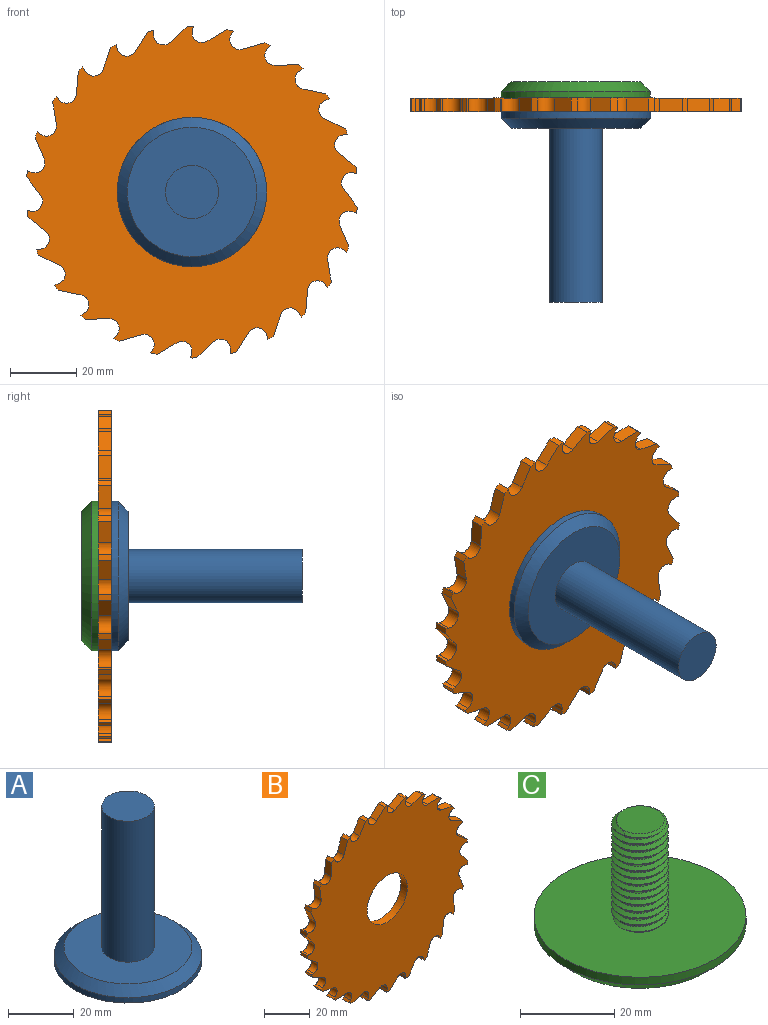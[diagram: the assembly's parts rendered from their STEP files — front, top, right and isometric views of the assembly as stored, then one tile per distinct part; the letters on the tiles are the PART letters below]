
ASSEMBLY  parts=3 mates=4
PART A: 15 faces, bbox 45.5x45.5x61.2 mm
  f0: plane 25.52x25.52mm, normal (0,0,-1), area 393.9mm2, adj f1,f9,f10,f11,f13
  f1: cylinder r=12.5mm len=25mm, axis (0,0,-1), area 196.3mm2, adj f0,f7
  f2: cone r=6mm half-angle=60deg, axis (0,0,-1), area 130.6mm2, adj f8,f12
  f3: plane 16x16mm, normal (0,0,1), area 201.1mm2, adj f4
  f4: cylinder r=8mm len=52.5mm, axis (0,0,-1), area 2638.9mm2, adj f3,f5
  f5: plane 39x39mm, normal (0,0,1), area 993.5mm2, adj f4,f14
  f6: cylinder r=22.5mm len=45mm, axis (0,0,-1), area 282.7mm2, adj f7,f14
  f7: plane 45x45mm, normal (0,0,-1), area 1099.6mm2, adj f1,f6
  f8: plane 6.23x1.47mm, normal (0,0,-1), area 0.6mm2, adj f2,f9,f10,f11
  f9: bspline ~31.17x14.02mm, area 657.5mm2, adj f0,f8,f11,f12,f13
  f10: bspline ~31.46x14.02mm, area 661.4mm2, adj f0,f8,f11,f12,f13
  f11: bspline ~30.55x14.21mm, area 166.2mm2, adj f0,f8,f9,f10
  f12: plane 12.44x11.91mm, normal (0,0,1), area 16.7mm2, adj f2,f9,f10,f13
  f13: cylinder r=5.12mm len=30mm, axis (0,0,1), area 392.2mm2, adj f0,f9,f10,f12
  f14: cone r=22.5mm half-angle=45deg, axis (0,0,-1), area 559.8mm2, adj f5,f6
PART B: 107 faces, bbox 99.6x4x100 mm
  f0: cylinder r=3mm len=5.31mm, axis (0,1,0), area 28.3mm2, adj f1,f104,f105,f106
  f1: plane 4x1.26mm, normal (-0.1,0,0.99), area 5.1mm2, adj f0,f2,f105,f106
  f2: cylinder r=50mm len=4mm, axis (0,1,0), area 7.6mm2, adj f1,f3,f105,f106
  f3: plane 6.28x4mm, normal (-0.43,0,-0.9), area 27.8mm2, adj f2,f4,f105,f106
  f4: cylinder r=3mm len=5.54mm, axis (0,1,0), area 28.3mm2, adj f3,f5,f105,f106
  f5: plane 4x1.19mm, normal (-0.34,0,0.94), area 5.1mm2, adj f4,f6,f105,f106
  f6: cylinder r=50mm len=4mm, axis (0,1,0), area 7.6mm2, adj f5,f7,f105,f106
  f7: plane 6.82x4mm, normal (-0.2,0,-0.98), area 27.8mm2, adj f6,f8,f105,f106
  f8: cylinder r=3mm len=5.44mm, axis (0,1,0), area 28.3mm2, adj f7,f9,f105,f106
  f9: plane 4x1.06mm, normal (-0.55,0,0.83), area 5.1mm2, adj f8,f10,f105,f106
  f10: cylinder r=50mm len=4mm, axis (0,1,0), area 7.6mm2, adj f9,f11,f105,f106
  f11: plane 6.95x4mm, normal (0.04,0,-1), area 27.8mm2, adj f10,f12,f105,f106
  f12: cylinder r=3mm len=5.03mm, axis (0,1,0), area 28.3mm2, adj f11,f13,f105,f106
  f13: plane 4x0.93mm, normal (-0.74,0,0.68), area 5.1mm2, adj f12,f14,f105,f106
  f14: cylinder r=50mm len=4mm, axis (0,1,0), area 7.6mm2, adj f13,f15,f105,f106
  f15: plane 6.68x4mm, normal (0.28,0,-0.96), area 27.8mm2, adj f14,f16,f105,f106
  f16: cylinder r=3mm len=4.45mm, axis (0,1,0), area 28.3mm2, adj f15,f17,f105,f106
  f17: plane 4x1.11mm, normal (-0.88,0,0.48), area 5.1mm2, adj f16,f18,f105,f106
  f18: cylinder r=50mm len=4mm, axis (0,1,0), area 7.6mm2, adj f17,f19,f105,f106
  f19: plane 6.02x4mm, normal (0.5,0,-0.87), area 27.8mm2, adj f18,f20,f105,f106
  f20: cylinder r=3mm len=4.5mm, axis (0,1,0), area 28.3mm2, adj f19,f21,f105,f106
  f21: plane 4x1.22mm, normal (-0.97,0,0.26), area 5.1mm2, adj f20,f22,f105,f106
  f22: cylinder r=50mm len=4mm, axis (0,1,0), area 7.6mm2, adj f21,f23,f105,f106
  f23: plane 5.02x4.82mm, normal (0.69,0,-0.72), area 27.8mm2, adj f22,f24,f105,f106
  f24: cylinder r=3mm len=5.08mm, axis (0,1,0), area 28.3mm2, adj f23,f25,f105,f106
  f25: plane 4x1.26mm, normal (-1,0,0.02), area 5.1mm2, adj f24,f26,f105,f106
  f26: cylinder r=50mm len=4mm, axis (0,1,0), area 7.6mm2, adj f25,f27,f105,f106
  f27: plane 5.88x4mm, normal (0.85,0,-0.53), area 27.8mm2, adj f26,f28,f105,f106
  f28: cylinder r=3mm len=5.46mm, axis (0,1,0), area 28.3mm2, adj f27,f29,f105,f106
  f29: plane 4x1.23mm, normal (-0.98,0,-0.22), area 5.1mm2, adj f28,f30,f105,f106
  f30: cylinder r=50mm len=4mm, axis (0,1,0), area 7.6mm2, adj f29,f31,f105,f106
  f31: plane 6.6x4mm, normal (0.95,0,-0.32), area 27.8mm2, adj f30,f32,f105,f106
  f32: cylinder r=3mm len=5.53mm, axis (0,1,0), area 28.3mm2, adj f31,f33,f105,f106
  f33: plane 4x1.13mm, normal (-0.89,0,-0.45), area 5.1mm2, adj f32,f34,f105,f106
  f34: cylinder r=50mm len=4mm, axis (0,1,0), area 7.6mm2, adj f33,f35,f105,f106
  f35: plane 6.93x4mm, normal (1,0,-0.08), area 27.8mm2, adj f34,f36,f105,f106
  f36: cylinder r=3mm len=5.28mm, axis (0,1,0), area 28.3mm2, adj f35,f37,f105,f106
  f37: plane 4x0.96mm, normal (-0.76,0,-0.65), area 5.1mm2, adj f36,f38,f105,f106
  f38: cylinder r=50mm len=4mm, axis (0,1,0), area 7.6mm2, adj f37,f39,f105,f106
  f39: plane 6.87x4mm, normal (0.99,0,0.16), area 27.8mm2, adj f38,f40,f105,f106
  f40: cylinder r=3mm len=4.75mm, axis (0,1,0), area 28.3mm2, adj f39,f41,f105,f106
  f41: plane 4x1.03mm, normal (-0.58,0,-0.81), area 5.1mm2, adj f40,f42,f105,f106
  f42: cylinder r=50mm len=4mm, axis (0,1,0), area 7.6mm2, adj f41,f43,f105,f106
  f43: plane 6.4x4mm, normal (0.92,0,0.39), area 27.8mm2, adj f42,f44,f105,f106
  f44: cylinder r=3mm len=4.18mm, axis (0,1,0), area 28.3mm2, adj f43,f45,f105,f106
  f45: plane 4x1.17mm, normal (-0.37,0,-0.93), area 5.1mm2, adj f44,f46,f105,f106
  f46: cylinder r=50mm len=4mm, axis (0,1,0), area 7.6mm2, adj f45,f47,f105,f106
  f47: plane 5.56x4.18mm, normal (0.8,0,0.6), area 27.8mm2, adj f46,f48,f105,f106
  f48: cylinder r=3mm len=4.8mm, axis (0,1,0), area 28.3mm2, adj f47,f49,f105,f106
  f49: plane 4x1.25mm, normal (-0.14,0,-0.99), area 5.1mm2, adj f48,f50,f105,f106
  f50: cylinder r=50mm len=4mm, axis (0,1,0), area 7.6mm2, adj f49,f51,f105,f106
  f51: plane 5.39x4.4mm, normal (0.63,0,0.77), area 27.8mm2, adj f50,f52,f105,f106
  f52: cylinder r=3mm len=5.31mm, axis (0,1,0), area 28.3mm2, adj f51,f53,f105,f106
  f53: plane 4x1.26mm, normal (0.1,0,-0.99), area 5.1mm2, adj f52,f54,f105,f106
  f54: cylinder r=50mm len=4mm, axis (0,1,0), area 7.6mm2, adj f53,f55,f105,f106
  f55: plane 6.28x4mm, normal (0.43,0,0.9), area 27.8mm2, adj f54,f56,f105,f106
  f56: cylinder r=3mm len=5.54mm, axis (0,1,0), area 28.3mm2, adj f55,f57,f105,f106
  f57: plane 4x1.19mm, normal (0.34,0,-0.94), area 5.1mm2, adj f56,f58,f105,f106
  f58: cylinder r=50mm len=4mm, axis (0,1,0), area 7.6mm2, adj f57,f59,f105,f106
  f59: plane 6.82x4mm, normal (0.2,0,0.98), area 27.8mm2, adj f58,f60,f105,f106
  f60: cylinder r=3mm len=5.44mm, axis (0,1,0), area 28.3mm2, adj f59,f61,f105,f106
  f61: plane 4x1.06mm, normal (0.55,0,-0.83), area 5.1mm2, adj f60,f62,f105,f106
  f62: cylinder r=50mm len=4mm, axis (0,1,0), area 7.6mm2, adj f61,f63,f105,f106
  f63: plane 6.95x4mm, normal (-0.04,0,1), area 27.8mm2, adj f62,f64,f105,f106
  f64: cylinder r=3mm len=5.03mm, axis (0,1,0), area 28.3mm2, adj f63,f65,f105,f106
  f65: plane 4x0.93mm, normal (0.74,0,-0.68), area 5.1mm2, adj f64,f66,f105,f106
  f66: cylinder r=50mm len=4mm, axis (0,1,0), area 7.6mm2, adj f65,f67,f105,f106
  f67: plane 6.68x4mm, normal (-0.28,0,0.96), area 27.8mm2, adj f66,f68,f105,f106
  f68: cylinder r=3mm len=4.45mm, axis (0,1,0), area 28.3mm2, adj f67,f69,f105,f106
  f69: plane 4x1.11mm, normal (0.88,0,-0.48), area 5.1mm2, adj f68,f70,f105,f106
  f70: cylinder r=50mm len=4mm, axis (0,1,0), area 7.6mm2, adj f69,f71,f105,f106
  f71: plane 6.02x4mm, normal (-0.5,0,0.87), area 27.8mm2, adj f70,f72,f105,f106
  f72: cylinder r=3mm len=4.5mm, axis (0,1,0), area 28.3mm2, adj f71,f73,f105,f106
  f73: plane 4x1.22mm, normal (0.97,0,-0.26), area 5.1mm2, adj f72,f74,f105,f106
  f74: cylinder r=50mm len=4mm, axis (0,1,0), area 7.6mm2, adj f73,f75,f105,f106
  f75: plane 5.02x4.82mm, normal (-0.69,0,0.72), area 27.8mm2, adj f74,f76,f105,f106
  f76: cylinder r=3mm len=5.08mm, axis (0,1,0), area 28.3mm2, adj f75,f77,f105,f106
  f77: plane 4x1.26mm, normal (1,0,-0.02), area 5.1mm2, adj f76,f78,f105,f106
  f78: cylinder r=50mm len=4mm, axis (0,1,0), area 7.6mm2, adj f77,f79,f105,f106
  f79: plane 5.88x4mm, normal (-0.85,0,0.53), area 27.8mm2, adj f78,f80,f105,f106
  f80: cylinder r=3mm len=5.46mm, axis (0,1,0), area 28.3mm2, adj f79,f81,f105,f106
  f81: plane 4x1.23mm, normal (0.98,0,0.22), area 5.1mm2, adj f80,f82,f105,f106
  f82: cylinder r=50mm len=4mm, axis (0,1,0), area 7.6mm2, adj f81,f83,f105,f106
  f83: plane 6.6x4mm, normal (-0.95,0,0.32), area 27.8mm2, adj f82,f84,f105,f106
  f84: cylinder r=3mm len=5.53mm, axis (0,1,0), area 28.3mm2, adj f83,f85,f105,f106
  f85: plane 4x1.13mm, normal (0.89,0,0.45), area 5.1mm2, adj f84,f86,f105,f106
  f86: cylinder r=50mm len=4mm, axis (0,1,0), area 7.6mm2, adj f85,f87,f105,f106
  f87: plane 6.93x4mm, normal (-1,0,0.08), area 27.8mm2, adj f86,f88,f105,f106
  f88: cylinder r=3mm len=5.28mm, axis (0,1,0), area 28.3mm2, adj f87,f89,f105,f106
  f89: plane 4x0.96mm, normal (0.76,0,0.65), area 5.1mm2, adj f88,f90,f105,f106
  f90: cylinder r=50mm len=4mm, axis (0,1,0), area 7.6mm2, adj f89,f91,f105,f106
  f91: plane 6.87x4mm, normal (-0.99,0,-0.16), area 27.8mm2, adj f90,f92,f105,f106
  f92: cylinder r=3mm len=4.75mm, axis (0,1,0), area 28.3mm2, adj f91,f93,f105,f106
  f93: plane 4x1.03mm, normal (0.58,0,0.81), area 5.1mm2, adj f92,f94,f105,f106
  f94: cylinder r=50mm len=4mm, axis (0,1,0), area 7.6mm2, adj f93,f95,f105,f106
  f95: plane 6.4x4mm, normal (-0.92,0,-0.39), area 27.8mm2, adj f94,f96,f105,f106
  f96: cylinder r=3mm len=4.18mm, axis (0,1,0), area 28.3mm2, adj f95,f97,f105,f106
  f97: plane 4x1.17mm, normal (0.37,0,0.93), area 5.1mm2, adj f96,f98,f105,f106
  f98: cylinder r=50mm len=4mm, axis (0,1,0), area 7.6mm2, adj f97,f99,f105,f106
  f99: plane 5.56x4.18mm, normal (-0.8,0,-0.6), area 27.8mm2, adj f98,f100,f105,f106
  f100: cylinder r=3mm len=4.8mm, axis (0,1,0), area 28.3mm2, adj f99,f101,f105,f106
  f101: plane 4x1.25mm, normal (0.14,0,0.99), area 5.1mm2, adj f100,f102,f105,f106
  f102: cylinder r=50mm len=4mm, axis (0,1,0), area 7.6mm2, adj f101,f104,f105,f106
  f103: cylinder r=12.5mm len=25mm, axis (0,1,0), area 314.2mm2, adj f105,f106
  f104: plane 5.39x4.4mm, normal (-0.63,0,-0.77), area 27.8mm2, adj f0,f102,f105,f106
  f105: plane 100x99.58mm, normal (0,-1,0), area 6496.4mm2, adj f0,f1,f2,f3,f4,f5,f6,f7
  f106: plane 100x99.58mm, normal (0,1,0), area 6496.4mm2, adj f0,f1,f2,f3,f4,f5,f6,f7
PART C: 10 faces, bbox 45.5x45.5x31.2 mm
  f0: cylinder r=6mm len=24.56mm, axis (0,0,-1), area 207.1mm2, adj f3,f7,f8,f9
  f1: plane 39x39mm, normal (0,0,-1), area 1194.6mm2, adj f5
  f2: plane 10.33x10.23mm, normal (0,0,1), area 81.4mm2, adj f6,f7,f8,f9
  f3: plane 45.49x45.49mm, normal (0,0,1), area 1496.6mm2, adj f0,f4,f6,f7,f8
  f4: cylinder r=22.5mm len=45mm, axis (0,0,-1), area 282.7mm2, adj f3,f5
  f5: cone r=19.5mm half-angle=45deg, axis (0,0,1), area 559.8mm2, adj f1,f4
  f6: bspline ~26.1x11.67mm, area 220.4mm2, adj f2,f3,f7,f8
  f7: bspline ~26.51x13.86mm, area 539.7mm2, adj f0,f2,f3,f6,f9
  f8: bspline ~25.92x13.86mm, area 536mm2, adj f0,f2,f3,f6,f9
  f9: cone r=6mm half-angle=63.4deg, axis (0,0,-1), area 13.9mm2, adj f0,f2,f7,f8
PLACE A rot(axis=(1,0,0),90deg) t=(-7.91,-17.25,25.55)mm
PLACE B t=(-7.91,-15.75,25.55)mm
PLACE C rot(axis=(1,0,0),90deg) t=(-7.94,-10.75,25.54)mm
MATE parallel C.f3 <-> B.f103  axis (0,-1,0) through (-7.91,-15.75,25.55)mm
MATE slider A.f1 <-> B.f103  axis (0,1,0) through (-7.91,-18.5,25.55)mm
MATE planar B.f103 <-> A.f1  axis (0,-1,0) through (-7.91,-19.75,25.55)mm
MATE parallel A.f1 <-> B.f103  axis (0,1,0) through (-7.91,-19.75,25.55)mm
